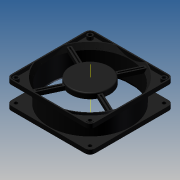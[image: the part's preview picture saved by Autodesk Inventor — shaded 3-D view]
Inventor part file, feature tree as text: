
AUTODESK INVENTOR PART (.ipt)
format: ipt  version: 2014 (Build 180170000, 170)  size: 357,888 bytes
history: native  units: mm (DEFAULTED — no unit token found)
features: sketch x11, extrude x7, fillet x3, plane x2, pattern_circular x2, revolve x1, hole x1, other x1, mirror x1
ambient origin geometry x8: Origin, YZ Plane, XZ Plane, XY Plane, X Axis, Y Axis, Z Axis, Center Point
bodies: Solid1 (feature_tree)
feature tree (29):
  revolve  "Revolution1"  [1 undecoded]
  plane  "Work Plane1"
  sketch  "Sketch2"  dims[d2=150.0deg d3=7.112mm]
  extrude  "Extrusion1"  Depth=7.112mm
  sketch  "Sketch3"  dims[d4=38.1mm d5=4.572mm d6=114.3mm d7=90.0deg]
  extrude  "Extrusion4"  Depth=4.572mm
  fillet  "Fillet2"  Radius=114.3mm
  fillet  "Fillet3"  [1 undecoded]
  extrude  "Extrusion5"  Depth=118.872mm
  extrude  "Extrusion6"  Depth=59.436mm
  hole  "Hole1"  [1 undecoded]
  other  "Work Axis1"
  pattern_circular  "Circular Pattern1"  [2 undecoded]
  mirror  "Mirror1"
  extrude  "Extrusion7"  Depth=3.048mm
  fillet  "Fillet4"  Radius=7.112mm
  sketch  "Sketch13"  dims[d17=1.016mm]
  plane  "Work Plane4"
  extrude  "Extrusion8"  Depth=3.048mm TaperAngle=0.0deg
  extrude  "Extrusion9"  Depth=3.048mm
  pattern_circular  "Circular Pattern2"  [2 undecoded]
  sketch  "Sketch1"  dims[d0=1.016mm d1=1.016mm]
  sketch  "Sketch6"  dims[d8=-19.05mm d9=118.872mm]
  sketch  "Sketch7"  dims[d10=118.872mm d11=59.436mm]
  sketch  "Sketch8"  dims[d12=59.436mm d13=25.4mm d14=0.0mm]
  sketch  "Sketch9"  dims[d15=1.016mm]
  sketch  "Sketch10"  dims[d16=1.016mm]
  sketch  "Sketch14"  dims[d18=1.016mm]
  sketch  "Sketch15"  dims[d27=1.778mm d28=6.096mm d29=0.0mm d30=5.08mm d31=7.112mm d32=0.762mm d33=0.0mm d34=7.62mm d35=4.7498mm d36=0.0mm d37=4.7498mm d38=12.7mm d39=9.525mm d40=6.35mm d41=14.3117mm d42=19.05mm d43=20.594885mm d44=40.0mm d46=360.0deg d47=55.88mm d48=7.62mm d49=0.0mm d50=1.524mm d51=5.588mm d52=3.048mm d53=5.588mm d54=3.048mm d55=0.0mm d56=3.048mm d57=0.0mm d58=40.0mm d60=360.0deg]
note: 7 required parameter values undecoded (feature->parameter linkage not recoverable at this tier; creation-order binding heuristic only, values carry confidence <= 0.55)